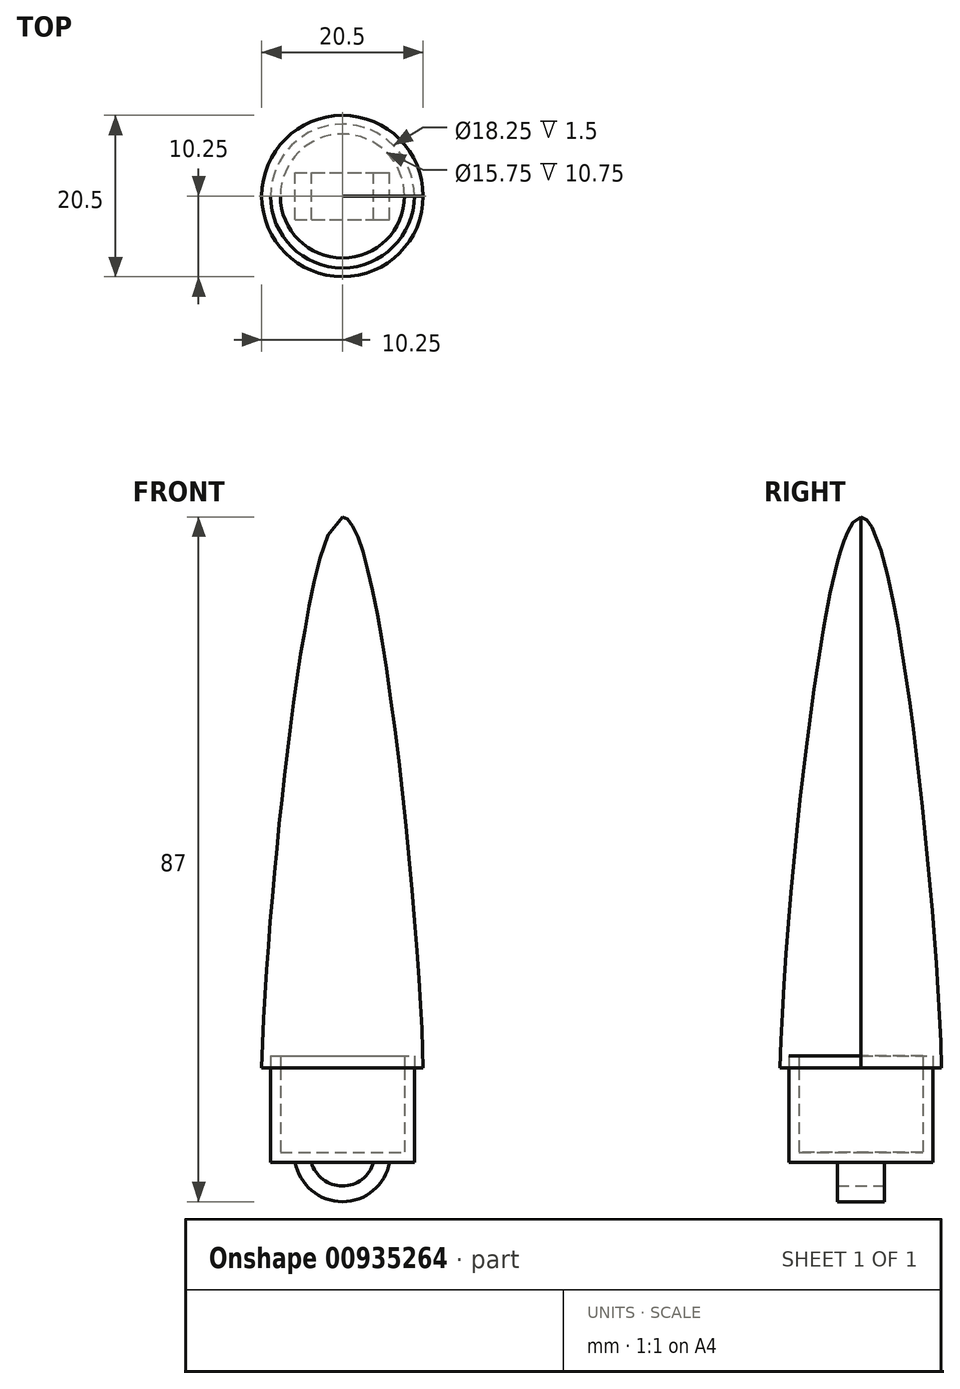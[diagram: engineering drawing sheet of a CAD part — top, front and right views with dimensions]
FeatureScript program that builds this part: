
annotation { "Feature Type Name" : "Feature", "Feature Type Description" : "" }
export const myFeature = defineFeature(function(context is Context, id is Id, definition is map)
    precondition{}
    {
        {
            var Q0;
            Q0=qCreatedBy(makeId("Front.planeOp"),FACE);
            var sketch = newSketch(context, id + "F0", { "sketchPlane" : qUnion([Q0])});
            skLineSegment(sketch, "E0", {"start": v(0, 0) * mm, "end": v(0, 70) * mm});
            skLineSegment(sketch, "E1", {"start": v(0, 0) * mm, "end": v(10.25, 0) * mm});
            skFitSpline(sketch, "E2", {"points": [v(0, 70) * mm, v(10.25, 0) * mm], "startDerivative": vector(15, 0) * mm, "endDerivative": vector(0.75, -48) * mm});
            skFitSpline(sketch, "E3.0", {"points": [v(-0.5, 68.7) * mm, v(-0.49, 68.7) * mm, v(-0.46, 68.67) * mm, v(-0.42, 68.64) * mm, v(-0.4, 68.62) * mm, v(-0.38, 68.61) * mm, v(-0.37, 68.6) * mm, v(-0.37, 68.6) * mm, v(-0.36, 68.6) * mm, v(-0.36, 68.6) * mm, v(-0.36, 68.6) * mm, v(-0.36, 68.6) * mm, v(-0.36, 68.6) * mm, v(-0.36, 68.6) * mm, v(-0.35, 68.58) * mm, v(-0.32, 68.56) * mm, v(-0.28, 68.52) * mm, v(-0.22, 68.44) * mm, v(-0.13, 68.3) * mm, v(0.01, 68.08) * mm, v(0.2, 67.72) * mm, v(0.46, 67.15) * mm, v(0.8, 66.25) * mm, v(1.23, 64.93) * mm, v(1.65, 63.38) * mm, v(2.08, 61.62) * mm, v(2.64, 59.04) * mm, v(3.33, 55.39) * mm, v(4.12, 50.47) * mm, v(4.87, 45.16) * mm, v(5.58, 39.56) * mm, v(6.24, 33.82) * mm, v(7.03, 26.12) * mm, v(7.85, 16.74) * mm, v(8.52, 6.87) * mm, v(8.72, 1.89) * mm, v(8.75, -0.02) * mm]});
            skLineSegment(sketch, "E4.bottom", {"start": v(7.87, 1.5) * mm, "end": v(9.12, 1.5) * mm});
            skLineSegment(sketch, "E4.top", {"start": v(7.88, -12) * mm, "end": v(9.12, -12) * mm});
            skLineSegment(sketch, "E4.left", {"start": v(7.87, 1.5) * mm, "end": v(7.87, -12) * mm});
            skLineSegment(sketch, "E4.right", {"start": v(9.12, 1.5) * mm, "end": v(9.12, -12) * mm});
            skLineSegment(sketch, "E5.bottom", {"start": v(7.88, -12) * mm, "end": v(0, -12) * mm});
            skLineSegment(sketch, "E5.top", {"start": v(7.88, -10.75) * mm, "end": v(0, -10.75) * mm});
            skLineSegment(sketch, "E5.left", {"start": v(7.88, -12) * mm, "end": v(7.88, -10.75) * mm});
            skLineSegment(sketch, "E5.right", {"start": v(0, -12) * mm, "end": v(0, -10.75) * mm});
            skSolve(sketch);
        }
        {
            var Q0;
            {var subQ5=sQuery(id+"F0.wireOp",EDGE,"E2");Q0=makeQuery(id+"F0.imprint","IMPRINT",FACE,{"disambiguationData":[TD([[makeQuery(id+"F0.imprint","IMPRINT",EDGE,{"derivedFrom":subQ5}),-1.0]])]});}
            var Q1;
            {var subQ0=sQuery(id+"F0.wireOp",EDGE,"E3.0");var subQ1=sQuery(id+"F0.wireOp",EDGE,"E1");var subQ2=makeQuery(id+"F0.imprint","INTERSECT",VERTEX,{"derivedFrom":[subQ1,subQ0]});Q1=makeQuery(id+"F0.imprint","IMPRINT",FACE,{"disambiguationData":[TD([[makeQuery(id+"F0.imprint","IMPRINT",EDGE,{"disambiguationData":[TD([[subQ2,1.0]])],"derivedFrom":subQ1}),1.0]])]});}
            var Q2;
            {var subQ0=sQuery(id+"F0.wireOp",EDGE,"E3.0");var subQ1=sQuery(id+"F0.wireOp",EDGE,"E1");var subQ2=makeQuery(id+"F0.imprint","INTERSECT",VERTEX,{"derivedFrom":[subQ1,subQ0]});Q2=makeQuery(id+"F0.imprint","IMPRINT",FACE,{"disambiguationData":[TD([[makeQuery(id+"F0.imprint","IMPRINT",EDGE,{"disambiguationData":[TD([[subQ2,-1.0]])],"derivedFrom":subQ1}),1.0]])]});}
            var Q3;
            {var subQ0=sQuery(id+"F0.wireOp",EDGE,"E4.top");Q3=makeQuery(id+"F0.imprint","IMPRINT",FACE,{"disambiguationData":[TD([[makeQuery(id+"F0.imprint","IMPRINT",EDGE,{"derivedFrom":subQ0}),1.0]])]});}
            var Q4;
            Q4=makeQuery(id+"F0.imprint","IMPRINT",FACE,{"disambiguationData":[TD([[makeQuery(id+"F0.imprint","IMPRINT",EDGE,{"derivedFrom":sQuery(id+"F0.wireOp",EDGE,"E5.bottom")}),-1.0]])]});
            var Q5;
            Q5=sQuery(id+"F0.wireOp",EDGE,"E0");
            revolve(context, id + "F1", {"surfaceOperationType" : NewSurfaceOperationType.NEW, "entities" : qUnion([Q0, Q1, Q2, Q3, Q4]), "axis" : qUnion([Q5]), "revolveType" : RevolveType.FULL});
        }
        {
            var Q0;
            Q0=qCreatedBy(makeId("Front.planeOp"),FACE);
            var sketch = newSketch(context, id + "F2", { "sketchPlane" : qUnion([Q0])});
            skArc(sketch, "E6", {"start": v(-6, -12) * mm, "mid": v(0, -17) * mm, "end": v(6, -12) * mm});
            skArc(sketch, "E7.0", {"start": v(-3.95, -12) * mm, "mid": v(0, -15) * mm, "end": v(3.95, -12) * mm});
            skLineSegment(sketch, "E8", {"start": v(-6, -12) * mm, "end": v(6, -12) * mm});
            skSolve(sketch);
        }
        {
            var Q0;
            {var subQ0=sQuery(id+"F2.wireOp",EDGE,"E6");Q0=makeQuery(id+"F2.imprint","IMPRINT",FACE,{"disambiguationData":[TD([[makeQuery(id+"F2.imprint","IMPRINT",EDGE,{"derivedFrom":subQ0}),1.0]])]});}
            extrude(context, id + "F3", {"entities" : qUnion([Q0]), "operationType" : NewBodyOperationType.ADD, "endBound" : BoundingType.SYMMETRIC, "depth" : 6 * mm, "offsetDistance" : 25 * mm});
        }
    });
